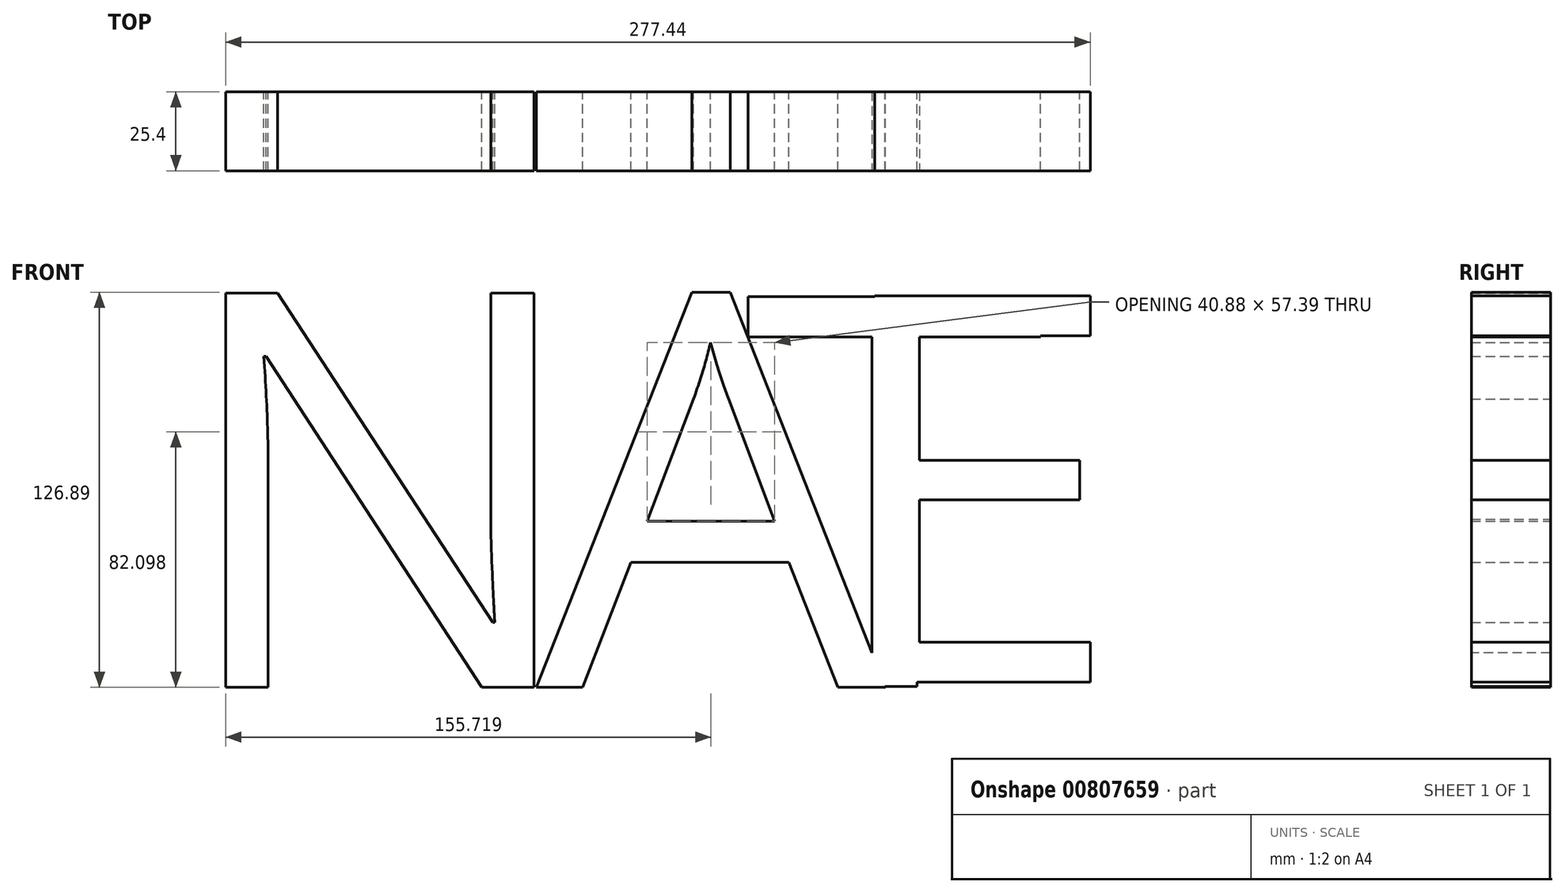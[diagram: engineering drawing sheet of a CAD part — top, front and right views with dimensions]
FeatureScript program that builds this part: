
annotation { "Feature Type Name" : "Feature", "Feature Type Description" : "" }
export const myFeature = defineFeature(function(context is Context, id is Id, definition is map)
    precondition{}
    {
        {
            var Q0;
            Q0=qCreatedBy(makeId("Front.planeOp"),FACE);
            var sketch = newSketch(context, id + "F0", { "sketchPlane" : qUnion([Q0])});
            skText(sketch, "E0", { "text": "A", "fontName": "OpenSans-Regular.ttf"});
            const initialGuessF0  = {"E0": [0.00397, -0.0646, 1, 0, 0.12744]};
            skSetInitialGuess(sketch, initialGuessF0);
            skSolve(sketch);
        }
        {
            var Q0;
            Q0=qCreatedBy(makeId("Front.planeOp"),FACE);
            var sketch = newSketch(context, id + "F1", { "sketchPlane" : qUnion([Q0])});
            skText(sketch, "E1", { "text": "T\n", "fontName": "OpenSans-Regular.ttf"});
            const initialGuessF1  = {"E1": [0.07045, -0.06431, 1, 0, 0.12628]};
            skSetInitialGuess(sketch, initialGuessF1);
            skSolve(sketch);
        }
        {
            var Q0;
            Q0=qCreatedBy(makeId("Front.planeOp"),FACE);
            var sketch = newSketch(context, id + "F2", { "sketchPlane" : qUnion([Q0])});
            skText(sketch, "E2", { "text": "E\n", "fontName": "OpenSans-Regular.ttf"});
            const initialGuessF2  = {"E2": [0.09548, -0.063, 1, 0, 0.12521]};
            skSetInitialGuess(sketch, initialGuessF2);
            skSolve(sketch);
        }
        {
            var Q0;
            Q0=makeQuery(id+"F0.imprint","IMPRINT",FACE,{"disambiguationData":[TD([[makeQuery(id+"F0.imprint","IMPRINT",EDGE,{"derivedFrom":sQuery(id+"F0.wireOp",EDGE,"E0.sketch_text.stroke-0")}),-1.0]])]});
            extrude(context, id + "F3", {"entities" : qUnion([Q0]), "depth" : 25.4 * mm, "offsetDistance" : 25.4 * mm});
        }
        {
            var Q0;
            Q0=makeQuery(id+"F1.imprint","IMPRINT",FACE,{"disambiguationData":[TD([[makeQuery(id+"F1.imprint","IMPRINT",EDGE,{"derivedFrom":sQuery(id+"F1.wireOp",EDGE,"E1.sketch_text.stroke-0")}),-1.0]])]});
            extrude(context, id + "F4", {"entities" : qUnion([Q0]), "operationType" : NewBodyOperationType.ADD, "depth" : 25.4 * mm, "offsetDistance" : 25.4 * mm});
        }
        {
            var Q0;
            Q0=makeQuery(id+"F2.imprint","IMPRINT",FACE,{"disambiguationData":[TD([[makeQuery(id+"F2.imprint","IMPRINT",EDGE,{"derivedFrom":sQuery(id+"F2.wireOp",EDGE,"E2.sketch_text.stroke-0")}),-1.0]])]});
            extrude(context, id + "F5", {"entities" : qUnion([Q0]), "operationType" : NewBodyOperationType.ADD, "depth" : 25.4 * mm, "offsetDistance" : 25.4 * mm});
        }
        {
            var Q0;
            Q0=qCreatedBy(makeId("Front.planeOp"),FACE);
            var sketch = newSketch(context, id + "F6", { "sketchPlane" : qUnion([Q0])});
            skText(sketch, "E3", { "text": "N", "fontName": "OpenSans-Regular.ttf"});
            const initialGuessF6  = {"E3": [-0.1131, -0.0646, 1, 0, 0.12772]};
            skSetInitialGuess(sketch, initialGuessF6);
            skSolve(sketch);
        }
        {
            var Q0;
            Q0=makeQuery(id+"F6.imprint","IMPRINT",FACE,{"disambiguationData":[TD([[makeQuery(id+"F6.imprint","IMPRINT",EDGE,{"derivedFrom":sQuery(id+"F6.wireOp",EDGE,"E3.sketch_text.stroke-0")}),-1.0]])]});
            extrude(context, id + "F7", {"entities" : qUnion([Q0]), "depth" : 25.4 * mm, "offsetDistance" : 25.4 * mm});
        }
    });
